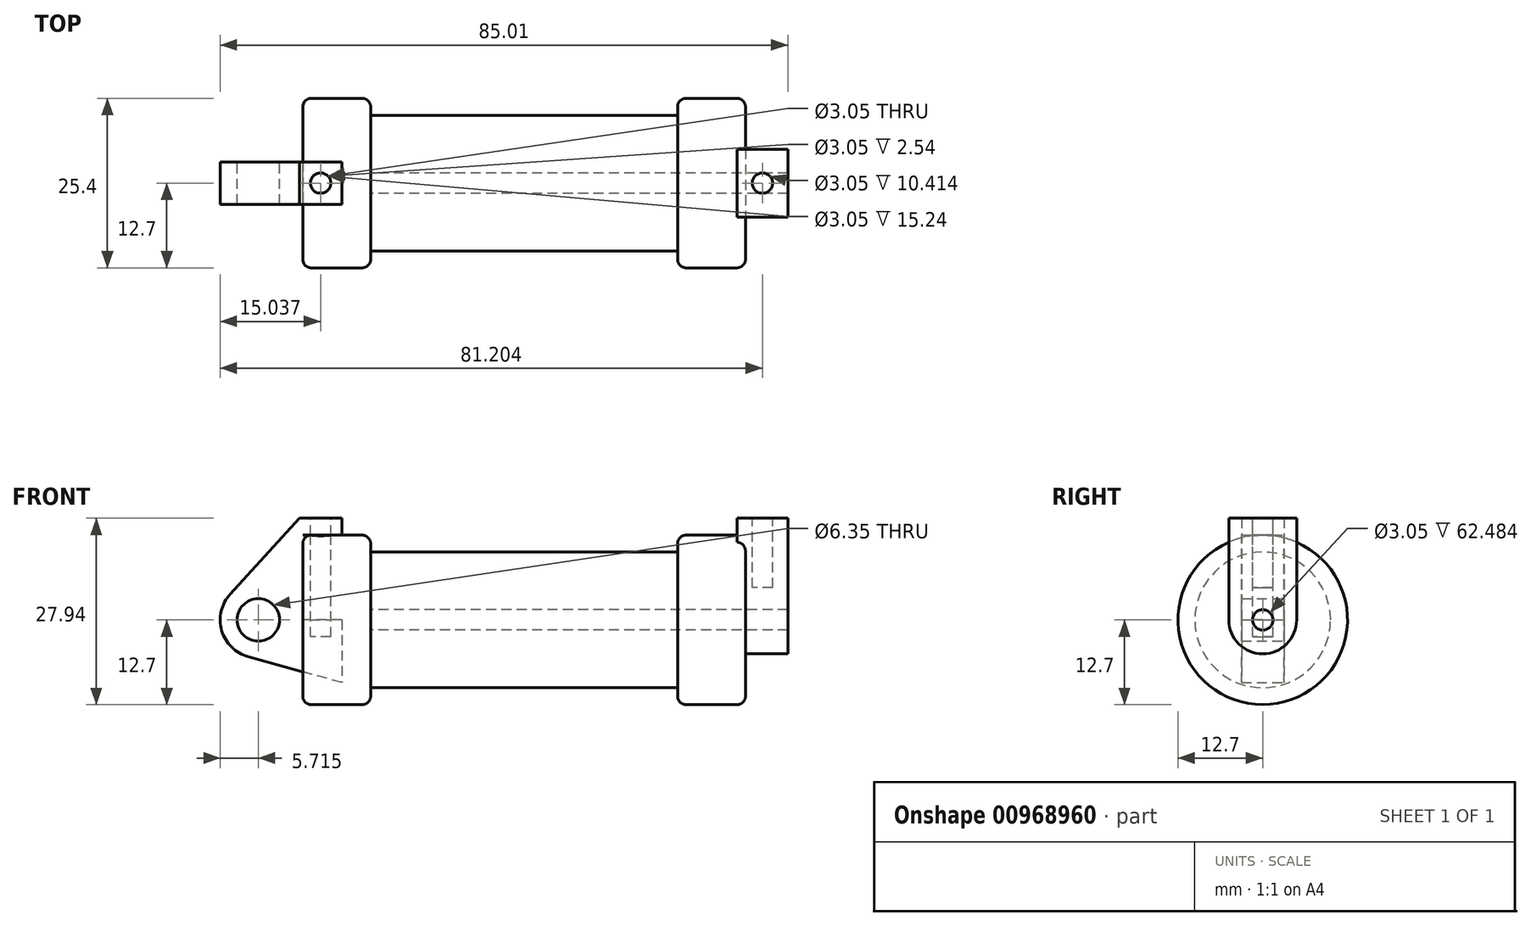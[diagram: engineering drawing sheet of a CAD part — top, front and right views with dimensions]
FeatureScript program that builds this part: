
annotation { "Feature Type Name" : "Feature", "Feature Type Description" : "" }
export const myFeature = defineFeature(function(context is Context, id is Id, definition is map)
    precondition{}
    {
        {
            var Q0;
            Q0=qCreatedBy(makeId("Front.planeOp"),FACE);
            var sketch = newSketch(context, id + "F0", { "sketchPlane" : qUnion([Q0])});
            skLineSegment(sketch, "E0", {"start": v(0, 0) * mm, "end": v(0, 12.7) * mm});
            skLineSegment(sketch, "E1", {"start": v(0, 12.7) * mm, "end": v(10.16, 12.7) * mm});
            skLineSegment(sketch, "E2", {"start": v(10.16, 12.7) * mm, "end": v(10.16, 10.16) * mm});
            skLineSegment(sketch, "E3", {"start": v(10.16, 10.16) * mm, "end": v(56.13, 10.16) * mm});
            skLineSegment(sketch, "E4", {"start": v(56.13, 10.16) * mm, "end": v(56.13, 12.7) * mm});
            skLineSegment(sketch, "E5", {"start": v(56.13, 12.7) * mm, "end": v(66.3, 12.7) * mm});
            skLineSegment(sketch, "E6", {"start": v(66.3, 12.7) * mm, "end": v(66.3, 0) * mm});
            skLineSegment(sketch, "E7", {"start": v(66.3, 0) * mm, "end": v(0, 0) * mm});
            skLineSegment(sketch, "E8", {"start": v(5.84, 15.24) * mm, "end": v(-0.5, 15.24) * mm});
            skLineSegment(sketch, "E9", {"start": v(-0.5, 15.24) * mm, "end": v(-10.88, 3.85) * mm});
            skLineSegment(sketch, "E10", {"start": v(0, 0) * mm, "end": v(-6.65, 0) * mm});
            skCircle(sketch, "E11", {"center": v(-6.65, 0) * mm, "radius": 5.72 * mm});
            skCircle(sketch, "E12", {"center": v(-6.65, 0) * mm, "radius": 3.18 * mm});
            skLineSegment(sketch, "E13", {"start": v(5.84, 15.24) * mm, "end": v(5.84, -9.4) * mm});
            skLineSegment(sketch, "E14", {"start": v(5.84, -9.4) * mm, "end": v(-8.18, -5.5) * mm});
            skSolve(sketch);
        }
        {
            var Q0;
            {var subQ0=sQuery(id+"F0.wireOp",EDGE,"E2");Q0=makeQuery(id+"F0.imprint","IMPRINT",FACE,{"disambiguationData":[TD([[makeQuery(id+"F0.imprint","IMPRINT",EDGE,{"derivedFrom":subQ0}),-1.0]])]});}
            var Q1;
            {var subQ0=sQuery(id+"F0.wireOp",EDGE,"E0");Q1=makeQuery(id+"F0.imprint","IMPRINT",FACE,{"disambiguationData":[TD([[makeQuery(id+"F0.imprint","IMPRINT",EDGE,{"derivedFrom":subQ0}),-1.0]])]});}
            var Q2;
            Q2=sQuery(id+"F0.wireOp",EDGE,"E7");
            revolve(context, id + "F1", {"surfaceOperationType" : NewSurfaceOperationType.NEW, "entities" : qUnion([Q0, Q1]), "axis" : qUnion([Q2]), "revolveType" : RevolveType.FULL});
        }
        {
            var Q0;
            {var subQ0=sQuery(id+"F0.wireOp",EDGE,"E14");Q0=makeQuery(id+"F0.imprint","IMPRINT",FACE,{"disambiguationData":[TD([[makeQuery(id+"F0.imprint","IMPRINT",EDGE,{"derivedFrom":subQ0}),-1.0]])]});}
            var Q1;
            {var subQ5=sQuery(id+"F0.wireOp",EDGE,"E12");Q1=makeQuery(id+"F0.imprint","IMPRINT",FACE,{"disambiguationData":[TD([[makeQuery(id+"F0.imprint","IMPRINT",EDGE,{"derivedFrom":subQ5}),-1.0]])]});}
            var Q2;
            {var subQ1=sQuery(id+"F0.wireOp",EDGE,"E0");Q2=makeQuery(id+"F0.imprint","IMPRINT",FACE,{"disambiguationData":[TD([[makeQuery(id+"F0.imprint","IMPRINT",EDGE,{"derivedFrom":subQ1}),1.0]])]});}
            extrude(context, id + "F2", {"entities" : qUnion([Q0, Q1, Q2]), "depth" : 3.17 * mm, "offsetDistance" : 25.4 * mm, "hasSecondDirection" : true, "secondDirectionOppositeDirection" : true, "secondDirectionDepth" : 3.17 * mm});
        }
        {
            var Q0;
            Q0=makeQuery(id+"F1.opRevolve","SWEPT_FACE",FACE,{"disambiguationData":[OSD([sQuery(id+"F0.wireOp",EDGE,"E6")])]});
            var sketch = newSketch(context, id + "F3", { "sketchPlane" : qUnion([Q0])});
            skCircle(sketch, "E15", {"center": v(0, 0) * mm, "radius": 5.08 * mm});
            skLineSegment(sketch, "E16", {"start": v(-5.08, 0) * mm, "end": v(-5.08, 15.24) * mm});
            skLineSegment(sketch, "E17", {"start": v(5.08, 15.24) * mm, "end": v(5.08, 0) * mm});
            skLineSegment(sketch, "E18", {"start": v(-5.08, 15.24) * mm, "end": v(5.08, 15.24) * mm});
            skCircle(sketch, "E19", {"center": v(0, 0) * mm, "radius": 1.52 * mm});
            skSolve(sketch);
        }
        {
            var Q0;
            {var subQ0=sQuery(id+"F3.wireOp",EDGE,"E18");Q0=makeQuery(id+"F3.imprint","IMPRINT",FACE,{"disambiguationData":[TD([[makeQuery(id+"F3.imprint","IMPRINT",EDGE,{"derivedFrom":subQ0}),-1.0]])]});}
            var Q1;
            {var subQ0=sQuery(id+"F3.wireOp",EDGE,"E16");var subQ1=sQuery(id+"F3.wireOp",EDGE,"E15");var subQ2=makeQuery(id+"F3.imprint","INTERSECT",VERTEX,{"derivedFrom":[subQ1,subQ0]});Q1=makeQuery(id+"F3.imprint","IMPRINT",FACE,{"disambiguationData":[TD([[makeQuery(id+"F3.imprint","IMPRINT",EDGE,{"disambiguationData":[TD([[subQ2,1.0]])],"derivedFrom":subQ1}),-1.0]])]});}
            var Q2;
            Q2=makeQuery(id+"F3.imprint","IMPRINT",FACE,{"disambiguationData":[TD([[makeQuery(id+"F3.imprint","IMPRINT",EDGE,{"derivedFrom":sQuery(id+"F3.wireOp",EDGE,"E19")}),-1.0]])]});
            extrude(context, id + "F4", {"entities" : qUnion([Q0, Q1, Q2]), "operationType" : NewBodyOperationType.ADD, "depth" : 6.35 * mm, "offsetDistance" : 25.4 * mm, "hasSecondDirection" : true, "secondDirectionOppositeDirection" : true, "secondDirectionDepth" : 1.27 * mm});
        }
        {
            var Q0;
            Q0=makeQuery(id+"F3.imprint","IMPRINT",FACE,{"disambiguationData":[TD([[makeQuery(id+"F3.imprint","IMPRINT",EDGE,{"derivedFrom":sQuery(id+"F3.wireOp",EDGE,"E19")}),1.0]])]});
            extrude(context, id + "F5", {"entities" : qUnion([Q0]), "operationType" : NewBodyOperationType.REMOVE, "oppositeDirection" : true, "depth" : 56.13 * mm, "offsetDistance" : 25.4 * mm});
        }
        {
            var Q0;
            Q0=makeQuery(id+"F2.opExtrude","SWEPT_FACE",FACE,{"disambiguationData":[OSD([sQuery(id+"F0.wireOp",EDGE,"E8")])]});
            var sketch = newSketch(context, id + "F6", { "sketchPlane" : qUnion([Q0])});
            skCircle(sketch, "E20", {"center": v(2.67, 0) * mm, "radius": 1.52 * mm});
            skSolve(sketch);
        }
        {
            var Q0;
            Q0=makeQuery(id+"F4.opExtrude","SWEPT_FACE",FACE,{"disambiguationData":[OSD([sQuery(id+"F3.wireOp",EDGE,"E18")])]});
            var sketch = newSketch(context, id + "F7", { "sketchPlane" : qUnion([Q0])});
            skCircle(sketch, "E21", {"center": v(68.83, 0) * mm, "radius": 1.52 * mm});
            skPoint(sketch, "E21.centerSnap0", {"position": v(72.64, 0) * mm});
            skSolve(sketch);
        }
        {
            var Q0;
            Q0=makeQuery(id+"F7.imprint","IMPRINT",FACE,{"disambiguationData":[TD([[makeQuery(id+"F7.imprint","IMPRINT",EDGE,{"derivedFrom":sQuery(id+"F7.wireOp",EDGE,"E21")}),1.0]])]});
            extrude(context, id + "F8", {"entities" : qUnion([Q0]), "operationType" : NewBodyOperationType.REMOVE, "oppositeDirection" : true, "depth" : 10.4 * mm, "offsetDistance" : 25.4 * mm});
        }
        {
            var Q0;
            Q0=makeQuery(id+"F6.imprint","IMPRINT",FACE,{"disambiguationData":[TD([[makeQuery(id+"F6.imprint","IMPRINT",EDGE,{"derivedFrom":sQuery(id+"F6.wireOp",EDGE,"E20")}),1.0]])]});
            extrude(context, id + "F9", {"entities" : qUnion([Q0]), "operationType" : NewBodyOperationType.REMOVE, "oppositeDirection" : true, "depth" : 17.78 * mm, "offsetDistance" : 25.4 * mm});
        }
        {
            var Q0;
            Q0=makeQuery(id+"F1.opRevolve","SWEPT_EDGE",EDGE,{"disambiguationData":[OSD([sQuery(id+"F0.wireOp",EDGE,"E0"),sQuery(id+"F0.wireOp",EDGE,"E1")])]});
            var Q1;
            Q1=makeQuery(id+"F1.opRevolve","SWEPT_EDGE",EDGE,{"disambiguationData":[OSD([sQuery(id+"F0.wireOp",EDGE,"E1"),sQuery(id+"F0.wireOp",EDGE,"E2")])]});
            var Q2;
            Q2=makeQuery(id+"F1.opRevolve","SWEPT_EDGE",EDGE,{"disambiguationData":[OSD([sQuery(id+"F0.wireOp",EDGE,"E4"),sQuery(id+"F0.wireOp",EDGE,"E5")])]});
            var Q3;
            Q3=makeQuery(id+"F1.opRevolve","SWEPT_EDGE",EDGE,{"disambiguationData":[OSD([sQuery(id+"F0.wireOp",EDGE,"E5"),sQuery(id+"F0.wireOp",EDGE,"E6")])]});
            fillet(context, id + "F10", {"entities" : qUnion([Q0, Q1, Q2, Q3]), "radius" : 1.27 * mm, "tangentPropagation" : true, "allowEdgeOverflow" : false});
        }
    });
